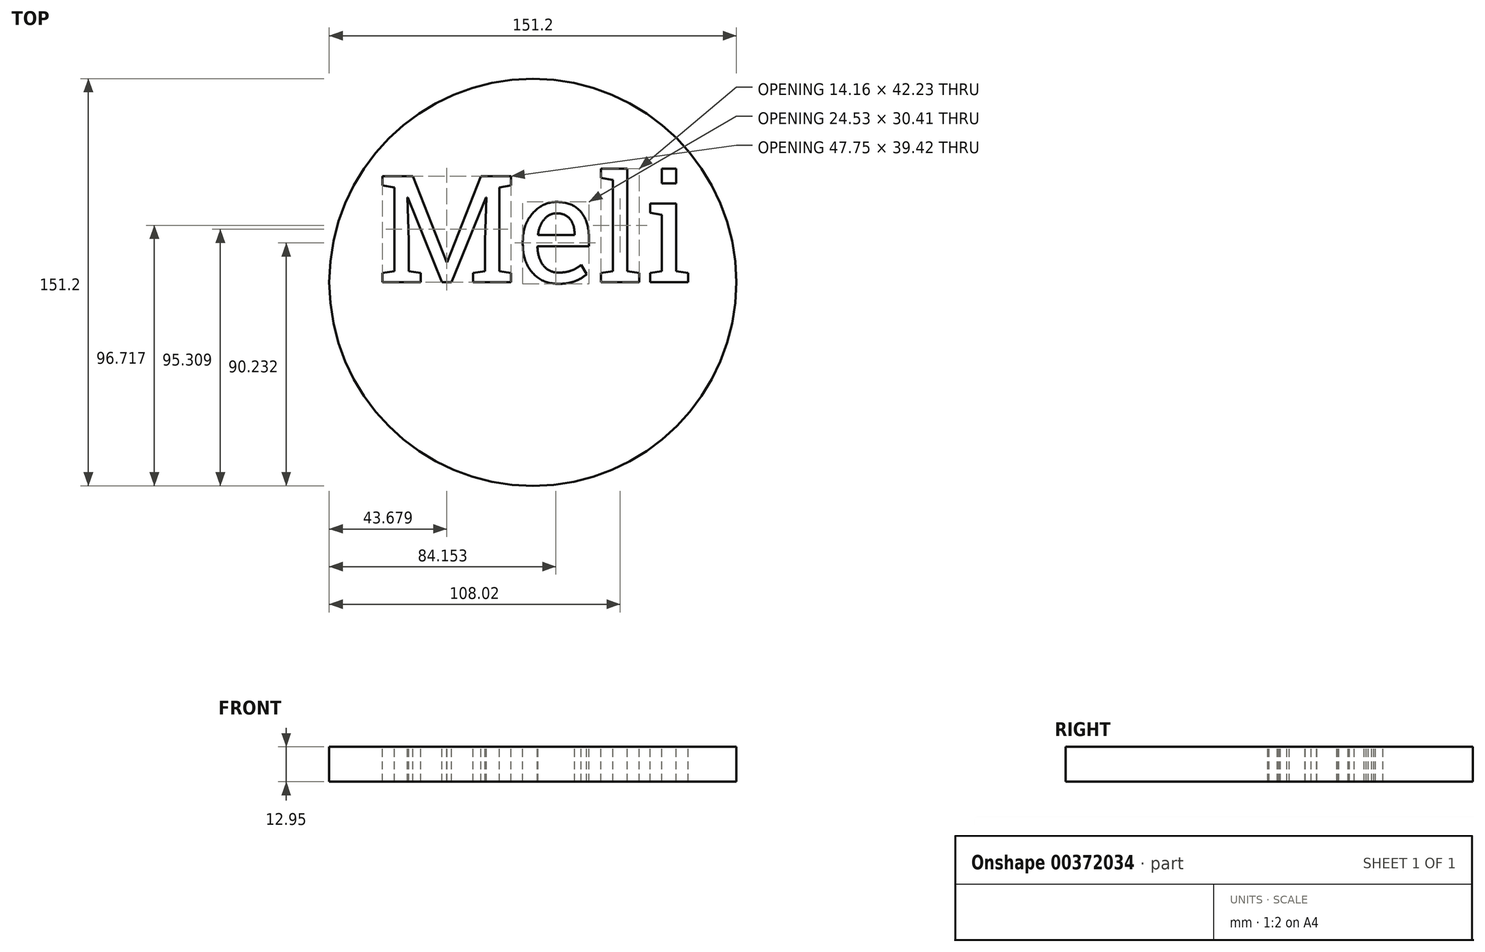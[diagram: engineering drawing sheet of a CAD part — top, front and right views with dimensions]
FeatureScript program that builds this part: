
annotation { "Feature Type Name" : "Feature", "Feature Type Description" : "" }
export const myFeature = defineFeature(function(context is Context, id is Id, definition is map)
    precondition{}
    {
        {
            var Q0;
            Q0=qCreatedBy(makeId("Top.planeOp"),FACE);
            var sketch = newSketch(context, id + "F0", { "sketchPlane" : qUnion([Q0])});
            skCircle(sketch, "E0", {"center": v(0, 0) * mm, "radius": 75.6 * mm});
            skSolve(sketch);
        }
        {
            var Q0;
            Q0=makeQuery(id+"F0.imprint","IMPRINT",FACE,{"disambiguationData":[TD([[makeQuery(id+"F0.imprint","IMPRINT",EDGE,{"derivedFrom":sQuery(id+"F0.wireOp",EDGE,"E0")}),1.0]])]});
            extrude(context, id + "F1", {"entities" : qUnion([Q0]), "depth" : 12.95 * mm});
        }
        {
            var Q0;
            Q0=makeQuery(id+"F1.opExtrude","CAP_FACE",FACE,{"disambiguationData":[OSD([sQuery(id+"F0.wireOp",EDGE,"E0")])],"isStart":false});
            var sketch = newSketch(context, id + "F2", { "sketchPlane" : qUnion([Q0])});
            skSolve(sketch);
        }
        {
            var Q0;
            Q0=makeQuery(id+"F2.imprint","IMPRINT",FACE,{"disambiguationData":[TD([[makeQuery(id+"F2.imprint","IMPRINT",EDGE,{"derivedFrom":makeQuery(id+"F1.opExtrude","CAP_EDGE",EDGE,{"disambiguationData":[OSD([sQuery(id+"F0.wireOp",EDGE,"E0")])],"isStart":false})}),1.0]])]});
            var sketch = newSketch(context, id + "F3", { "sketchPlane" : qUnion([Q0])});
            skText(sketch, "E1", { "text": "Meli", "fontName": "RobotoSlab-Regular.ttf"});
            const initialGuessF3  = {"E1": [-0.05772, 0, 1, 0, 0.03992]};
            skSetInitialGuess(sketch, initialGuessF3);
            skSolve(sketch);
        }
        {
            var Q0;
            Q0 = qSketchRegion(id + "F3", true);
            extrude(context, id + "F4", {"entities" : qUnion([Q0]), "operationType" : NewBodyOperationType.REMOVE, "oppositeDirection" : true, "depth" : 29.72 * mm});
        }
    });
